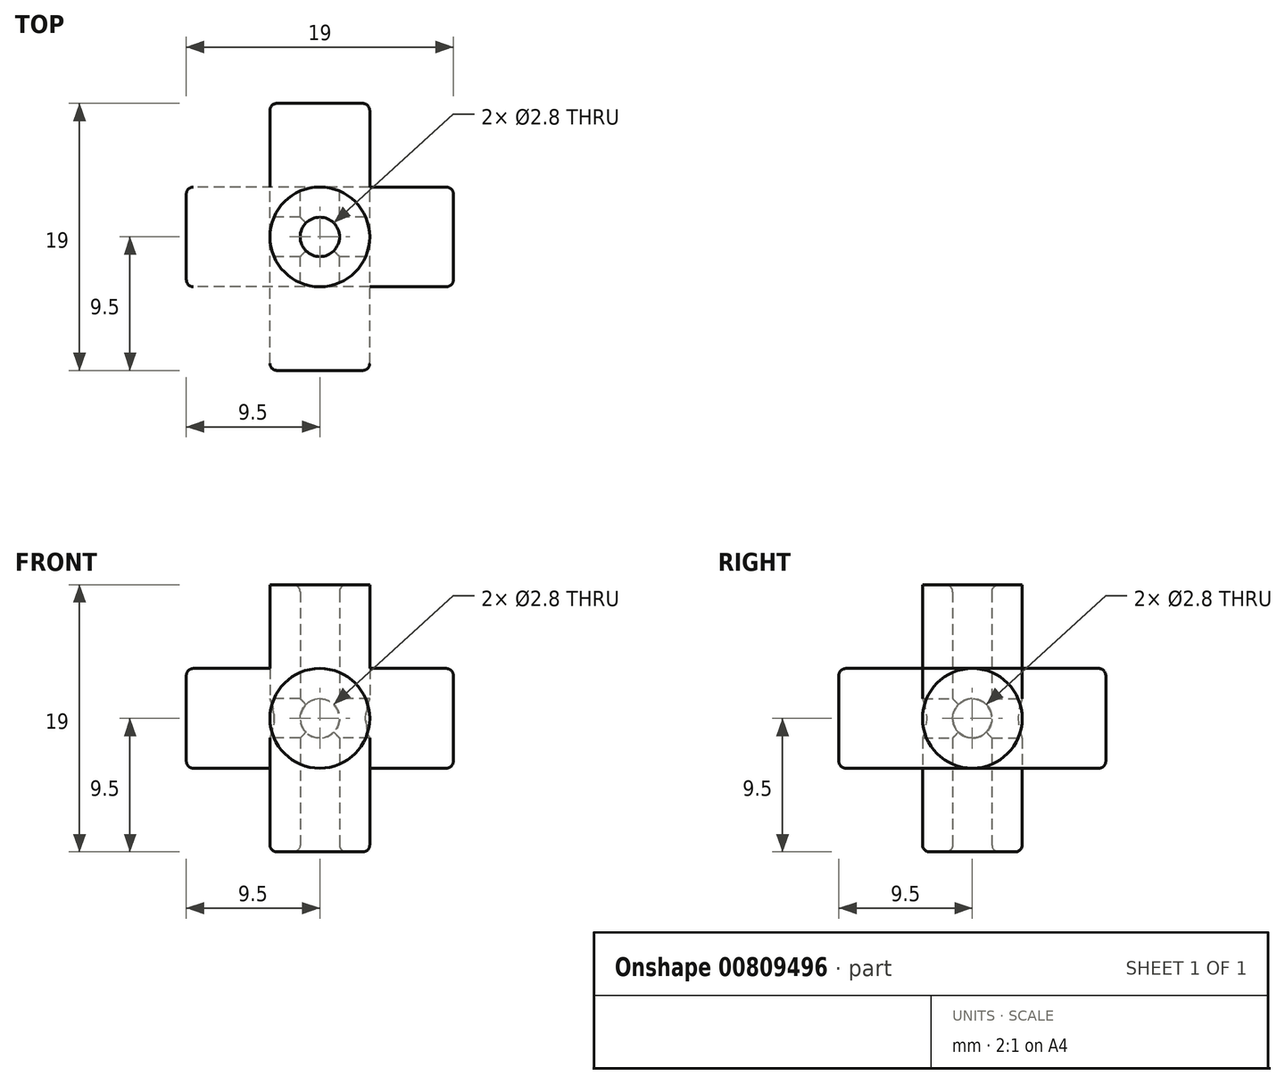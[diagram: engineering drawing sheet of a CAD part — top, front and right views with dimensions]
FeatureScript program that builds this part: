
annotation { "Feature Type Name" : "Feature", "Feature Type Description" : "" }
export const myFeature = defineFeature(function(context is Context, id is Id, definition is map)
    precondition{}
    {
        {
            var Q0;
            Q0=qCreatedBy(makeId("Front.planeOp"),FACE);
            var sketch = newSketch(context, id + "F0", { "sketchPlane" : qUnion([Q0])});
            skCircle(sketch, "E0", {"center": v(0, 0) * mm, "radius": 3.55 * mm});
            skSolve(sketch);
        }
        {
            var Q0;
            Q0=makeQuery(id+"F0.imprint","IMPRINT",FACE,{"disambiguationData":[TD([[makeQuery(id+"F0.imprint","IMPRINT",EDGE,{"derivedFrom":sQuery(id+"F0.wireOp",EDGE,"E0")}),1.0]])]});
            extrude(context, id + "F1", {"entities" : qUnion([Q0]), "endBound" : BoundingType.SYMMETRIC, "depth" : 19 * mm, "offsetDistance" : 25 * mm});
        }
        {
            var Q0;
            Q0=qCreatedBy(makeId("Front.planeOp"),FACE);
            var sketch = newSketch(context, id + "F2", { "sketchPlane" : qUnion([Q0])});
            skCircle(sketch, "E1", {"center": v(0, 0) * mm, "radius": 1.4 * mm});
            skSolve(sketch);
        }
        {
            var Q0;
            Q0 = qSketchRegion(id + "F2", true);
            extrude(context, id + "F3", {"entities" : qUnion([Q0]), "endBound" : BoundingType.SYMMETRIC, "depth" : 20 * mm, "offsetDistance" : 25 * mm});
        }
        {
            var Q0;
            Q0=qCreatedBy(makeId("Front.planeOp"),FACE);
            var sketch = newSketch(context, id + "F4", { "sketchPlane" : qUnion([Q0])});
            skLineSegment(sketch, "E2.bottom", {"start": v(0, 0) * mm, "end": v(10, 0) * mm});
            skLineSegment(sketch, "E2.top", {"start": v(0, 10) * mm, "end": v(10, 10) * mm});
            skLineSegment(sketch, "E2.left", {"start": v(0, 0) * mm, "end": v(0, 10) * mm});
            skLineSegment(sketch, "E2.right", {"start": v(10, 0) * mm, "end": v(10, 10) * mm});
            skSolve(sketch);
        }
        {
            var Q0;
            Q0 = qSketchRegion(id + "F4", true);
            extrude(context, id + "F5", {"entities" : qUnion([Q0]), "depth" : 10 * mm, "offsetDistance" : 25 * mm});
        }
        {
            var Q0;
            Q0=qCreatedBy(makeId("Origin.pointOp"),VERTEX);
            var Q1;
            Q1=makeQuery(id+"F5.opExtrude","CAP_VERTEX",VERTEX,{"disambiguationData":[OSD([sQuery(id+"F4.wireOp",EDGE,"E2.top"),sQuery(id+"F4.wireOp",EDGE,"E2.right")])],"isStart":false});
            var Q2;
            Q2=makeQuery(id+"F5.opExtrude","CAP_VERTEX",VERTEX,{"disambiguationData":[OSD([sQuery(id+"F4.wireOp",EDGE,"E2.bottom"),sQuery(id+"F4.wireOp",EDGE,"E2.right")])],"isStart":false});
            cPlane(context, id + "F6", {"entities" : qUnion([Q0, Q1, Q2]), "cplaneType" : CPlaneType.THREE_POINT, "offset" : 25 * mm, "width" : 150 * mm, "height" : 150 * mm});
        }
        {
            var Q0;
            Q0=qCreatedBy(id+"F6.planeOp",FACE);
            var sketch = newSketch(context, id + "F7", { "sketchPlane" : qUnion([Q0])});
            skLineSegment(sketch, "E3", {"start": v(0, 0) * mm, "end": v(14.14, 10) * mm});
            skSolve(sketch);
        }
        {
            var Q0;
            Q0=makeQuery(id+"F5.opExtrude","SWEPT_BODY",BODY,{"disambiguationData":[OSD([sQuery(id+"F4.wireOp",EDGE,"E2.bottom"),sQuery(id+"F4.wireOp",EDGE,"E2.top"),sQuery(id+"F4.wireOp",EDGE,"E2.left"),sQuery(id+"F4.wireOp",EDGE,"E2.right")])]});
            deleteBodies(context, id + "F8", {"entities" : qUnion([Q0])});
        }
        {
            var Q0;
            Q0=makeQuery(id+"F3.opExtrude","SWEPT_BODY",BODY,{"disambiguationData":[OSD([sQuery(id+"F2.wireOp",EDGE,"E1")])]});
            var Q1;
            Q1=makeQuery(id+"F1.opExtrude","SWEPT_BODY",BODY,{"disambiguationData":[OSD([sQuery(id+"F0.wireOp",EDGE,"E0")])]});
            var Q2;
            Q2=sQuery(id+"F7.wireOp",EDGE,"E3");
            circularPattern(context, id + "F9", {"entities" : qUnion([Q0, Q1]), "axis" : qUnion([Q2]), "angle" : 360 * degree, "instanceCount" : 3, "equalSpace" : true});
        }
        {
            var Q0;
            Q0=makeQuery(id+"F3.opExtrude","SWEPT_BODY",BODY,{"disambiguationData":[OSD([sQuery(id+"F2.wireOp",EDGE,"E1")])]});
            var Q1;
            Q1=makeQuery(id+"F9.opPattern","COPY",BODY,{"derivedFrom":makeQuery(id+"F3.opExtrude","SWEPT_BODY",BODY,{"disambiguationData":[OSD([sQuery(id+"F2.wireOp",EDGE,"E1")])]}),"instanceName":"2"});
            var Q2;
            Q2=makeQuery(id+"F9.opPattern","COPY",BODY,{"derivedFrom":makeQuery(id+"F3.opExtrude","SWEPT_BODY",BODY,{"disambiguationData":[OSD([sQuery(id+"F2.wireOp",EDGE,"E1")])]}),"instanceName":"1"});
            var Q3;
            Q3=makeQuery(id+"F9.opPattern","COPY",BODY,{"derivedFrom":makeQuery(id+"F1.opExtrude","SWEPT_BODY",BODY,{"disambiguationData":[OSD([sQuery(id+"F0.wireOp",EDGE,"E0")])]}),"instanceName":"2"});
            booleanBodies(context, id + "F10", {"operationType" : BooleanOperationType.SUBTRACTION, "tools" : qUnion([Q0, Q1, Q2]), "targets" : qUnion([Q3])});
        }
        {
            var Q0;
            Q0=makeQuery(id+"F10.opBoolean","INTERSECT",EDGE,{"derivedFrom":[makeQuery(id+"F9.opPattern","COPY",FACE,{"derivedFrom":makeQuery(id+"F1.opExtrude","CAP_FACE",FACE,{"disambiguationData":[OSD([sQuery(id+"F0.wireOp",EDGE,"E0")])],"isStart":true}),"instanceName":"2"}),makeQuery(id+"F9.opPattern","COPY",FACE,{"derivedFrom":makeQuery(id+"F3.opExtrude","SWEPT_FACE",FACE,{"disambiguationData":[OSD([sQuery(id+"F2.wireOp",EDGE,"E1")])]}),"instanceName":"2"})]});
            var Q1;
            Q1=makeQuery(id+"F9.opPattern","COPY",FACE,{"derivedFrom":makeQuery(id+"F1.opExtrude","CAP_FACE",FACE,{"disambiguationData":[OSD([sQuery(id+"F0.wireOp",EDGE,"E0")])],"isStart":true}),"instanceName":"2"});
            var Q2;
            Q2=makeQuery(id+"F9.opPattern","COPY",FACE,{"derivedFrom":makeQuery(id+"F1.opExtrude","CAP_FACE",FACE,{"disambiguationData":[OSD([sQuery(id+"F0.wireOp",EDGE,"E0")])],"isStart":false}),"instanceName":"1"});
            var Q3;
            Q3=makeQuery(id+"F1.opExtrude","CAP_FACE",FACE,{"disambiguationData":[OSD([sQuery(id+"F0.wireOp",EDGE,"E0")])],"isStart":true});
            var Q4;
            Q4=makeQuery(id+"F9.opPattern","COPY",FACE,{"derivedFrom":makeQuery(id+"F1.opExtrude","CAP_FACE",FACE,{"disambiguationData":[OSD([sQuery(id+"F0.wireOp",EDGE,"E0")])],"isStart":true}),"instanceName":"1"});
            var Q5;
            Q5=makeQuery(id+"F1.opExtrude","CAP_FACE",FACE,{"disambiguationData":[OSD([sQuery(id+"F0.wireOp",EDGE,"E0")])],"isStart":false});
            var Q6;
            Q6=makeQuery(id+"F10.opBoolean","INTERSECT",EDGE,{"derivedFrom":[makeQuery(id+"F9.opPattern","COPY",FACE,{"derivedFrom":makeQuery(id+"F1.opExtrude","CAP_FACE",FACE,{"disambiguationData":[OSD([sQuery(id+"F0.wireOp",EDGE,"E0")])],"isStart":false}),"instanceName":"2"}),makeQuery(id+"F9.opPattern","COPY",FACE,{"derivedFrom":makeQuery(id+"F3.opExtrude","SWEPT_FACE",FACE,{"disambiguationData":[OSD([sQuery(id+"F2.wireOp",EDGE,"E1")])]}),"instanceName":"2"})]});
            fillet(context, id + "F11", {"entities" : qUnion([Q0, Q1, Q2, Q3, Q4, Q5, Q6]), "radius" : 0.5 * mm, "tangentPropagation" : true, "allowEdgeOverflow" : false});
        }
    });
